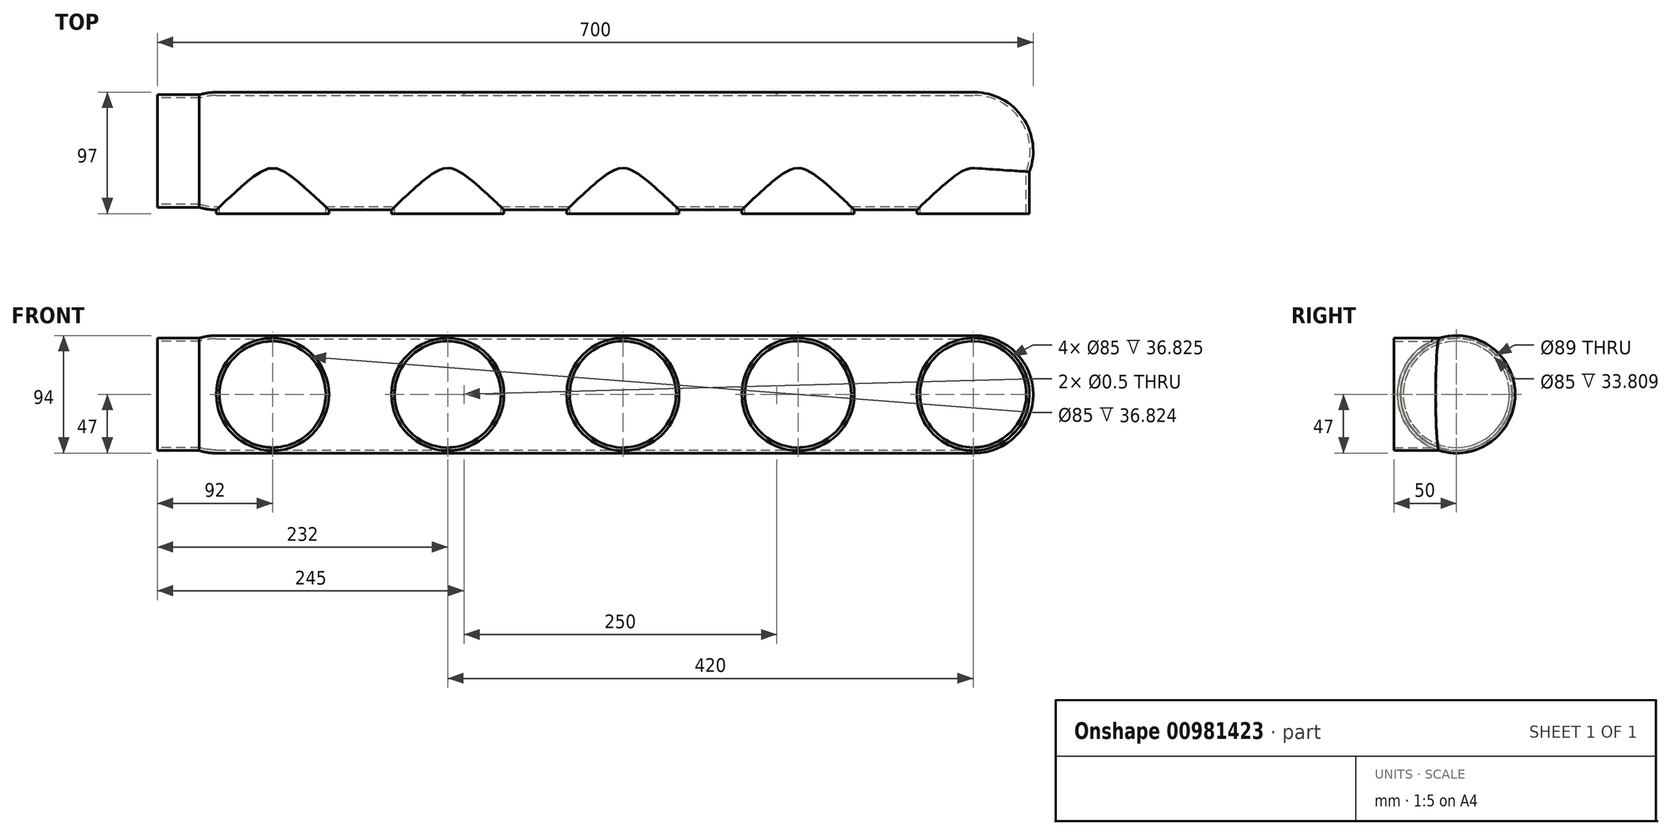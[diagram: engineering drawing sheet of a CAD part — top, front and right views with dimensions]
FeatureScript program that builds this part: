
annotation { "Feature Type Name" : "Feature", "Feature Type Description" : "" }
export const myFeature = defineFeature(function(context is Context, id is Id, definition is map)
    precondition{}
    {
        {
            var Q0;
            Q0=qCreatedBy(makeId("Front.planeOp"),FACE);
            var sketch = newSketch(context, id + "F0", { "sketchPlane" : qUnion([Q0])});
            skLineSegment(sketch, "E0.bottom", {"start": v(-350, 47) * mm, "end": v(350, 47) * mm});
            skLineSegment(sketch, "E0.top", {"start": v(-350, -47) * mm, "end": v(350, -47) * mm});
            skLineSegment(sketch, "E0.left", {"start": v(-350, 47) * mm, "end": v(-350, -47) * mm});
            skLineSegment(sketch, "E0.right", {"start": v(350, 47) * mm, "end": v(350, -47) * mm});
            skPoint(sketch, "E0.middle", {"position": v(0, 0) * mm});
            skSolve(sketch);
        }
        {
            var Q0;
            Q0=makeQuery(id+"F0.imprint","IMPRINT",FACE,{"disambiguationData":[TD([[makeQuery(id+"F0.imprint","IMPRINT",EDGE,{"derivedFrom":sQuery(id+"F0.wireOp",EDGE,"E0.bottom")}),-1.0]])]});
            extrude(context, id + "F1", {"entities" : qUnion([Q0]), "endBound" : BoundingType.SYMMETRIC, "depth" : 94 * mm, "offsetDistance" : 25 * mm});
        }
        {
            var Q0;
            Q0=makeQuery(id+"F1.opExtrude","SWEPT_FACE",FACE,{"disambiguationData":[OSD([sQuery(id+"F0.wireOp",EDGE,"E0.left")])]});
            cPlane(context, id + "F2", {"entities" : qUnion([Q0]), "cplaneType" : CPlaneType.OFFSET, "offset" : 0 * mm, "width" : 150 * mm, "height" : 150 * mm});
        }
        {
            var Q0;
            Q0=makeQuery(id+"F1.opExtrude","SWEPT_FACE",FACE,{"disambiguationData":[OSD([sQuery(id+"F0.wireOp",EDGE,"E0.bottom")])]});
            var Q1;
            Q1=makeQuery(id+"F1.opExtrude","CAP_FACE",FACE,{"disambiguationData":[OSD([sQuery(id+"F0.wireOp",EDGE,"E0.bottom"),sQuery(id+"F0.wireOp",EDGE,"E0.top"),sQuery(id+"F0.wireOp",EDGE,"E0.left"),sQuery(id+"F0.wireOp",EDGE,"E0.right")])],"isStart":false});
            var Q2;
            Q2=makeQuery(id+"F1.opExtrude","SWEPT_FACE",FACE,{"disambiguationData":[OSD([sQuery(id+"F0.wireOp",EDGE,"E0.top")])]});
            var Q3;
            Q3=makeQuery(id+"F1.opExtrude","CAP_FACE",FACE,{"disambiguationData":[OSD([sQuery(id+"F0.wireOp",EDGE,"E0.bottom"),sQuery(id+"F0.wireOp",EDGE,"E0.top"),sQuery(id+"F0.wireOp",EDGE,"E0.left"),sQuery(id+"F0.wireOp",EDGE,"E0.right")])],"isStart":true});
            var Q4;
            Q4=makeQuery(id+"F1.opExtrude","SWEPT_FACE",FACE,{"disambiguationData":[OSD([sQuery(id+"F0.wireOp",EDGE,"E0.right")])]});
            fillet(context, id + "F3", {"entities" : qUnion([Q0, Q1, Q2, Q3, Q4]), "radius" : 47 * mm, "tangentPropagation" : true, "allowEdgeOverflow" : false});
        }
        {
            var Q0;
            Q0=qCreatedBy(id+"F2.planeOp",FACE);
            var sketch = newSketch(context, id + "F4", { "sketchPlane" : qUnion([Q0])});
            skCircle(sketch, "E1", {"center": v(0, 0) * mm, "radius": 45 * mm});
            skSolve(sketch);
        }
        {
            var Q0;
            Q0=qSketchRegion(id+"F4",true);
            extrude(context, id + "F5", {"entities" : qUnion([Q0]), "operationType" : NewBodyOperationType.ADD, "oppositeDirection" : true, "depth" : 100 * mm, "offsetDistance" : 25 * mm});
        }
        {
            var Q0;
            Q0=qCreatedBy(makeId("Front.planeOp"),FACE);
            var sketch = newSketch(context, id + "F6", { "sketchPlane" : qUnion([Q0])});
            skCircle(sketch, "E2", {"center": v(22, 0) * mm, "radius": 45 * mm});
            skCircle(sketch, "E3", {"center": v(162, 0) * mm, "radius": 45 * mm});
            skCircle(sketch, "E4", {"center": v(302, 0) * mm, "radius": 45 * mm});
            skCircle(sketch, "E5", {"center": v(-258, 0) * mm, "radius": 45 * mm});
            skCircle(sketch, "E6", {"center": v(-118, 0) * mm, "radius": 45 * mm});
            skSolve(sketch);
        }
        {
            var Q0;
            Q0=qSketchRegion(id+"F6",true);
            extrude(context, id + "F7", {"entities" : qUnion([Q0]), "operationType" : NewBodyOperationType.ADD, "depth" : 50 * mm, "offsetDistance" : 25 * mm});
        }
        {
            var Q0;
            Q0=makeQuery(id+"F7.opExtrude","CAP_FACE",FACE,{"disambiguationData":[OSD([sQuery(id+"F6.wireOp",EDGE,"21sKYaGF-B368-Wwl2-OhkZ-wf8vG0b8O0Hr")])],"isStart":false});
            var Q1;
            Q1=makeQuery(id+"F7.opExtrude","CAP_FACE",FACE,{"disambiguationData":[OSD([sQuery(id+"F6.wireOp",EDGE,"aba59EDD-dIZK-h3VM-gZ2g-2MMW7iUeaAD7")])],"isStart":false});
            var Q2;
            Q2=makeQuery(id+"F7.opExtrude","CAP_FACE",FACE,{"disambiguationData":[OSD([sQuery(id+"F6.wireOp",EDGE,"E5")])],"isStart":false});
            var Q3;
            Q3=makeQuery(id+"F7.opExtrude","CAP_FACE",FACE,{"disambiguationData":[OSD([sQuery(id+"F6.wireOp",EDGE,"E6")])],"isStart":false});
            var Q4;
            Q4=makeQuery(id+"F7.opExtrude","CAP_FACE",FACE,{"disambiguationData":[OSD([sQuery(id+"F6.wireOp",EDGE,"E2")])],"isStart":false});
            var Q5;
            Q5=makeQuery(id+"F7.opExtrude","CAP_FACE",FACE,{"disambiguationData":[OSD([sQuery(id+"F6.wireOp",EDGE,"E3")])],"isStart":false});
            var Q6;
            Q6=makeQuery(id+"F7.opExtrude","CAP_FACE",FACE,{"disambiguationData":[OSD([sQuery(id+"F6.wireOp",EDGE,"E4")])],"isStart":false});
            var Q7;
            Q7=makeQuery(id+"F5.opExtrude","CAP_FACE",FACE,{"disambiguationData":[OSD([sQuery(id+"F4.wireOp",EDGE,"E1")])],"isStart":true});
            shell(context, id + "F8", {"entities" : qUnion([Q0, Q1, Q2, Q3, Q4, Q5, Q6, Q7]), "thickness" : 2.5 * mm});
        }
        {
            var Q0;
            Q0=qCreatedBy(makeId("Front.planeOp"),FACE);
            cPlane(context, id + "F9", {"entities" : qUnion([Q0]), "cplaneType" : CPlaneType.OFFSET, "offset" : 47 * mm, "oppositeDirection" : true, "width" : 150 * mm, "height" : 150 * mm});
        }
        {
            var Q0;
            Q0=qCreatedBy(id+"F9.planeOp",FACE);
            var sketch = newSketch(context, id + "F10", { "sketchPlane" : qUnion([Q0])});
            skPoint(sketch, "E7", {"position": v(145, 0) * mm});
            skPoint(sketch, "E8", {"position": v(-105, 0) * mm});
            skSolve(sketch);
        }
        {
            var Q0;
            Q0=sQuery(id+"F10.wireOp",VERTEX,"E7");
            var Q1;
            Q1=sQuery(id+"F10.wireOp",VERTEX,"E8");
            var Q2;
            Q2=makeQuery(id+"F1.opExtrude","SWEPT_BODY",BODY,{"disambiguationData":[OSD([sQuery(id+"F0.wireOp",EDGE,"E0.bottom"),sQuery(id+"F0.wireOp",EDGE,"E0.top"),sQuery(id+"F0.wireOp",EDGE,"E0.left"),sQuery(id+"F0.wireOp",EDGE,"E0.right")])]});
            hole(context, id + "F11", {"style" : HoleStyle.SIMPLE, "endStyle" : HoleEndStyle.BLIND, "oppositeDirection" : true, "holeDiameter" : 0.5 * mm, "majorDiameter" : 5 * mm, "holeDepth" : 50 * mm, "isTappedThrough" : true, "tappedDepth" : 12 * mm, "tapClearance" : 3, "startFromSketch" : true, "locations" : qUnion([Q0, Q1]), "scope" : qUnion([Q2])});
        }
    });
